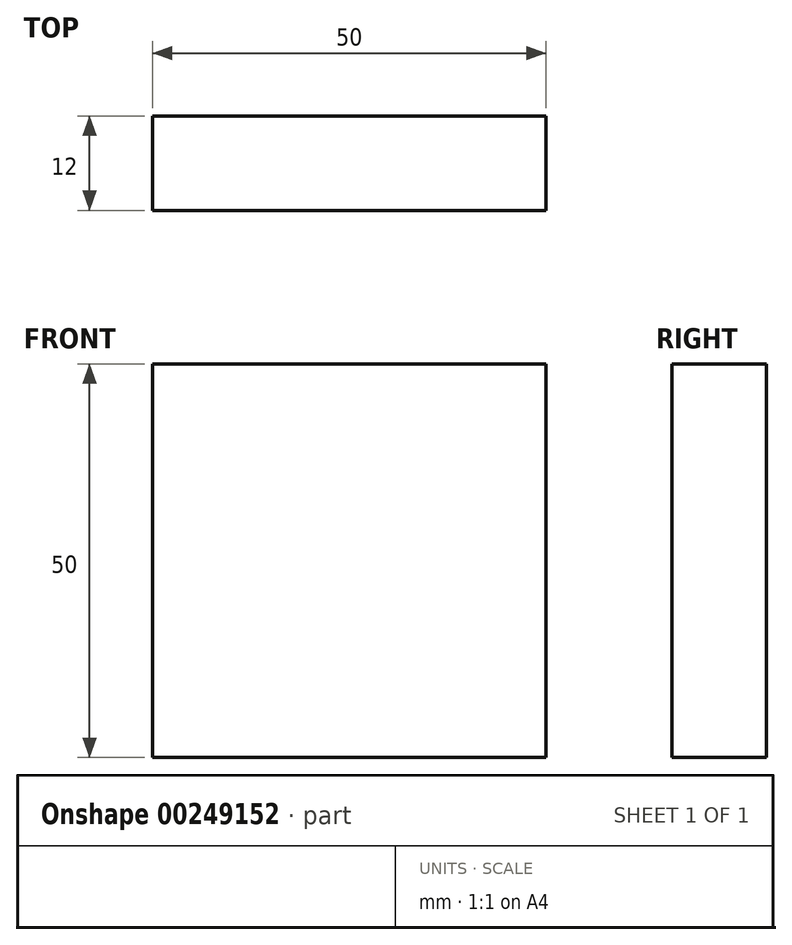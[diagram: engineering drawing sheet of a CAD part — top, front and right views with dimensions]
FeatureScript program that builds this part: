
annotation { "Feature Type Name" : "Feature", "Feature Type Description" : "" }
export const myFeature = defineFeature(function(context is Context, id is Id, definition is map)
    precondition{}
    {
        {
            var Q0;
            Q0=qCreatedBy(makeId("Front.planeOp"),FACE);
            var sketch = newSketch(context, id + "F0", { "sketchPlane" : qUnion([Q0])});
            skLineSegment(sketch, "E0.bottom", {"start": v(0, 0) * mm, "end": v(50, 0) * mm});
            skLineSegment(sketch, "E0.top", {"start": v(0, 50) * mm, "end": v(50, 50) * mm});
            skLineSegment(sketch, "E0.left", {"start": v(0, 0) * mm, "end": v(0, 50) * mm});
            skLineSegment(sketch, "E0.right", {"start": v(50, 0) * mm, "end": v(50, 50) * mm});
            skSolve(sketch);
        }
        {
            var Q0;
            Q0=makeQuery(id+"F0.imprint","IMPRINT",FACE,{"disambiguationData":[TD([[makeQuery(id+"F0.imprint","IMPRINT",EDGE,{"derivedFrom":sQuery(id+"F0.wireOp",EDGE,"E0.bottom")}),1.0]])]});
            extrude(context, id + "F1", {"entities" : qUnion([Q0]), "depth" : 12 * mm});
        }
    });
